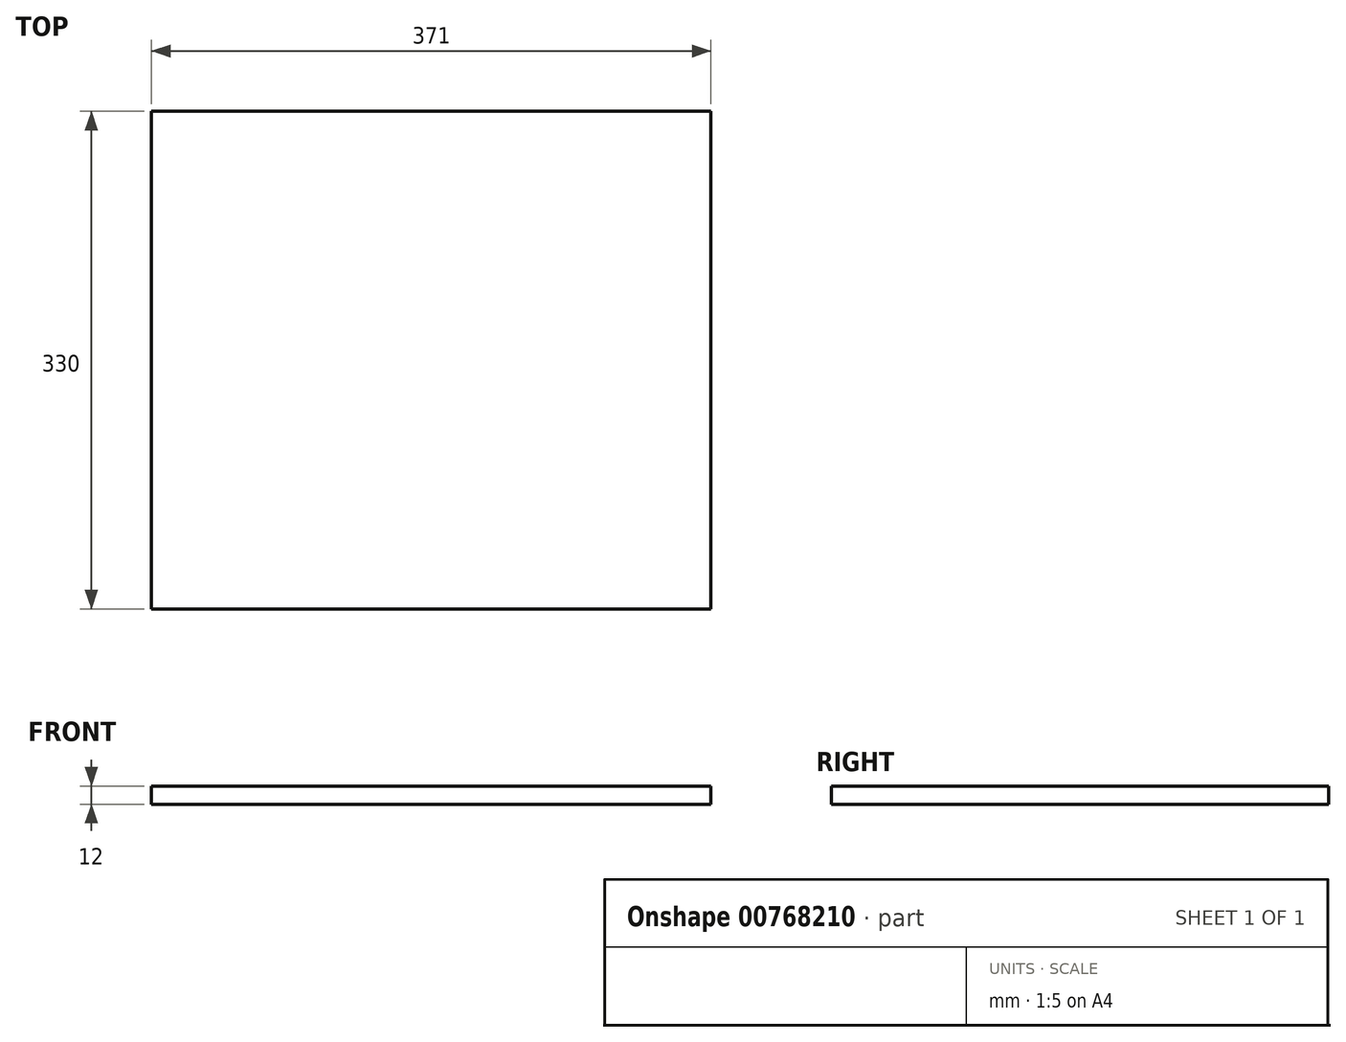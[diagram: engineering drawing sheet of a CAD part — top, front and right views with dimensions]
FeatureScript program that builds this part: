
annotation { "Feature Type Name" : "Feature", "Feature Type Description" : "" }
export const myFeature = defineFeature(function(context is Context, id is Id, definition is map)
    precondition{}
    {
        {
            var Q0;
            Q0=qCreatedBy(makeId("Top.planeOp"),FACE);
            var sketch = newSketch(context, id + "F0", { "sketchPlane" : qUnion([Q0])});
            skLineSegment(sketch, "E0.bottom", {"start": v(-70.96, 65.05) * mm, "end": v(300.04, 65.05) * mm});
            skLineSegment(sketch, "E0.top", {"start": v(-70.96, -264.95) * mm, "end": v(300.04, -264.95) * mm});
            skLineSegment(sketch, "E0.left", {"start": v(-70.96, 65.05) * mm, "end": v(-70.96, -264.95) * mm});
            skLineSegment(sketch, "E0.right", {"start": v(300.04, 65.05) * mm, "end": v(300.04, -264.95) * mm});
            skSolve(sketch);
        }
        {
            var Q0;
            Q0=qSketchRegion(id+"F0",true);
            extrude(context, id + "F1", {"entities" : qUnion([Q0]), "depth" : 12 * mm, "offsetDistance" : 25 * mm});
        }
    });
